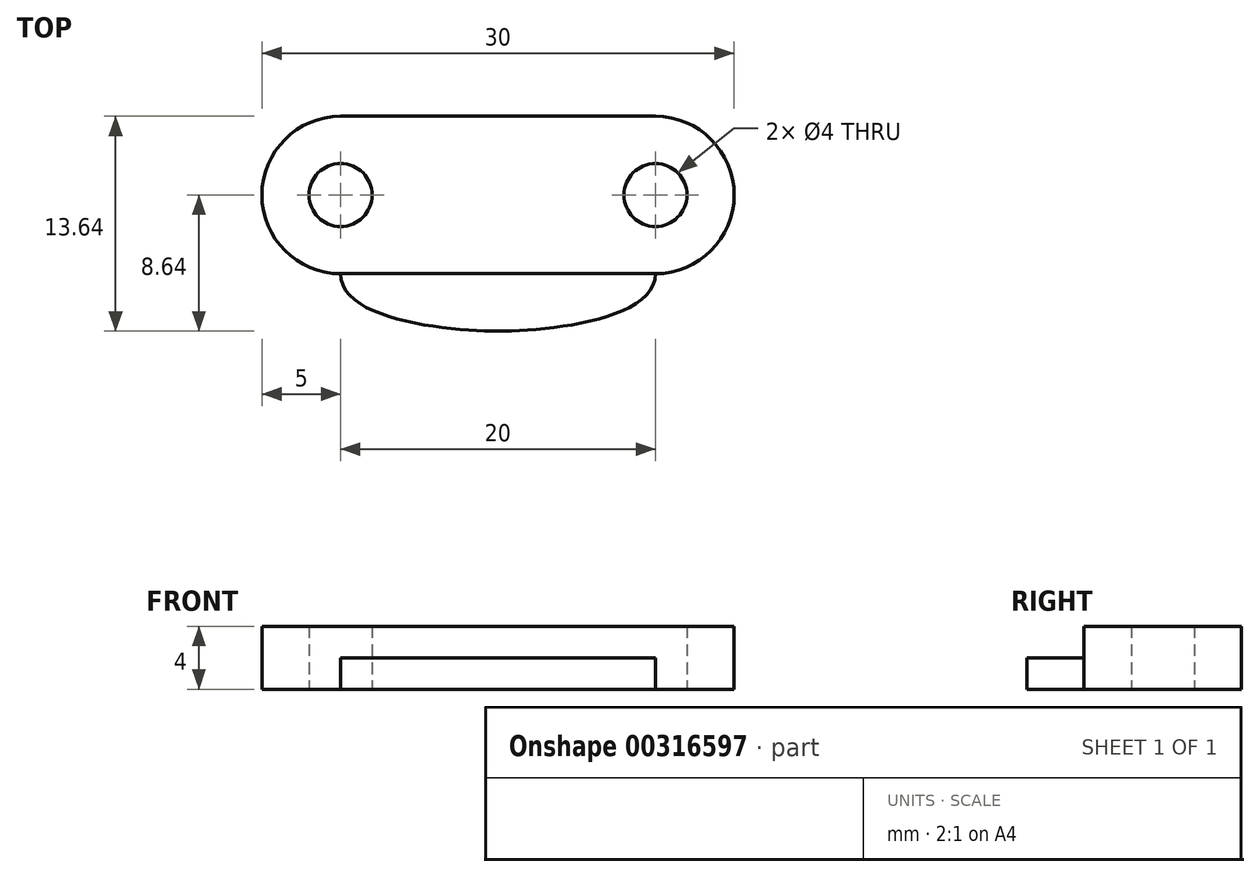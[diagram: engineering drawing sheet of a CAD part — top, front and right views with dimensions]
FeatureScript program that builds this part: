
annotation { "Feature Type Name" : "Feature", "Feature Type Description" : "" }
export const myFeature = defineFeature(function(context is Context, id is Id, definition is map)
    precondition{}
    {
        {
            var Q0;
            Q0=qCreatedBy(makeId("Top.planeOp"),FACE);
            var sketch = newSketch(context, id + "F0", { "sketchPlane" : qUnion([Q0])});
            skLineSegment(sketch, "E0", {"start": v(0, 10) * mm, "end": v(-10, 10) * mm});
            skLineSegment(sketch, "E1", {"start": v(-10, 10) * mm, "end": v(-10, 0) * mm, "construction": true});
            skArc(sketch, "E2", {"start": v(-10, 10) * mm, "mid": v(-15, 5) * mm, "end": v(-10, 0) * mm});
            skLineSegment(sketch, "E3", {"start": v(-10, 0) * mm, "end": v(0, -3.64) * mm, "construction": true});
            skFitSpline(sketch, "E4", {"points": [v(-10, 0) * mm, v(0, -3.64) * mm], "startDerivative": vector(0, -9) * mm, "endDerivative": vector(9, 0) * mm});
            skCircle(sketch, "E5", {"center": v(-10, 5) * mm, "radius": 2 * mm});
            skPoint(sketch, "E6.cCircle.centerSnap0", {"position": v(0, 5) * mm});
            skPoint(sketch, "E6.0.midPoint", {"position": v(0, 5) * mm});
            skLineSegment(sketch, "E7", {"start": v(0, 10) * mm, "end": v(0, 0) * mm, "construction": true});
            skLineSegment(sketch, "E8.MirrorCS", {"start": v(0, 10) * mm, "end": v(10, 10) * mm});
            skArc(sketch, "E9.MirrorCS", {"start": v(10, 10) * mm, "mid": v(15, 5) * mm, "end": v(10, 0) * mm});
            skFitSpline(sketch, "E10.MirrorCS", {"points": [v(10, 0) * mm, v(0, -3.64) * mm], "startDerivative": vector(0, -9) * mm, "endDerivative": vector(-9, 0) * mm});
            skCircle(sketch, "E11.MirrorC", {"center": v(10, 5) * mm, "radius": 2 * mm});
            skLineSegment(sketch, "E12", {"start": v(-10, 0) * mm, "end": v(10, 0) * mm});
            skSolve(sketch);
        }
        {
            var Q0;
            Q0=makeQuery(id+"F0.imprint","IMPRINT",FACE,{"disambiguationData":[TD([[makeQuery(id+"F0.imprint","IMPRINT",EDGE,{"derivedFrom":sQuery(id+"F0.wireOp",EDGE,"E4")}),1.0]])]});
            extrude(context, id + "F1", {"entities" : qUnion([Q0]), "depth" : 2 * mm});
        }
        {
            var Q0;
            Q0=makeQuery(id+"F0.imprint","IMPRINT",FACE,{"disambiguationData":[TD([[makeQuery(id+"F0.imprint","IMPRINT",EDGE,{"derivedFrom":sQuery(id+"F0.wireOp",EDGE,"E0")}),1.0]])]});
            extrude(context, id + "F2", {"entities" : qUnion([Q0]), "operationType" : NewBodyOperationType.ADD, "depth" : 4 * mm});
        }
    });
